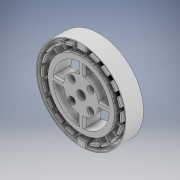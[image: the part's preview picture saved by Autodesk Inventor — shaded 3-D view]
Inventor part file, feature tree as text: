
AUTODESK INVENTOR PART (.ipt)
format: ipt  version: 2020 (Build 240168000, 168)  size: 632,320 bytes
history: native  units: mm
features: extrude x8, sketch x8, pattern_circular x1, fillet x1
ambient origin geometry x8: Origin, YZ Plane, XZ Plane, XY Plane, X Axis, Y Axis, Z Axis, Center Point
bodies: Solid1 (feature_tree)
feature tree (18):
  extrude  "Extrusion1"  Depth=20.0mm
  extrude  "Extrusion7"  Depth=4.0mm
  pattern_circular  "Circular Pattern2"  Count=4 Angle=360.0deg
  extrude  "Extrusion8"  Depth=10.0mm TaperAngle=0.0deg
  extrude  "Extrusion4"  Depth=1.0mm
  extrude  "Extrusion9"  Depth=50.0mm
  extrude  "Extrusion10"  Depth=10.0mm TaperAngle=0.0deg
  extrude  "Extrusion5"  Depth=4.0mm
  extrude  "Extrusion6"  Depth=1.0mm
  fillet  "Fillet1"  Radius=4.0mm
  sketch  "Sketch10"  dims[d33=40.0mm d35=360.0deg d37=15.0mm d38=4.0mm d39=40.0mm d41=360.0deg d43=15.0mm d44=0.0mm d45=10.0mm d46=0.0mm d47=10.0mm d48=0.0mm d49=200.0mm d50=360.0deg d52=2.0mm d53=1.0mm d54=0.0mm d55=200.0mm d57=360.0deg d59=2.5mm d60=0.0mm d61=200.0mm d63=360.0deg d65=2.5mm d66=0.0mm d67=1.0mm]
  sketch  "Sketch1"  dims[d0=38.0mm d1=20.0mm]
  sketch  "Sketch2"  dims[d2=5.0mm d5=4.0mm d6=40.0mm d8=360.0deg]
  sketch  "Sketch5"  dims[d10=40.0mm d12=360.0deg d14=10.0mm d15=0.0mm]
  sketch  "Sketch6"  dims[d18=1.0mm d19=4.0mm]
  sketch  "Sketch7"  dims[d23=32.0mm d27=50.0mm]
  sketch  "Sketch8"  dims[d28=51.0mm d29=10.0mm d30=0.0mm]
  sketch  "Sketch9"  dims[d31=135.0deg d32=4.0mm]
